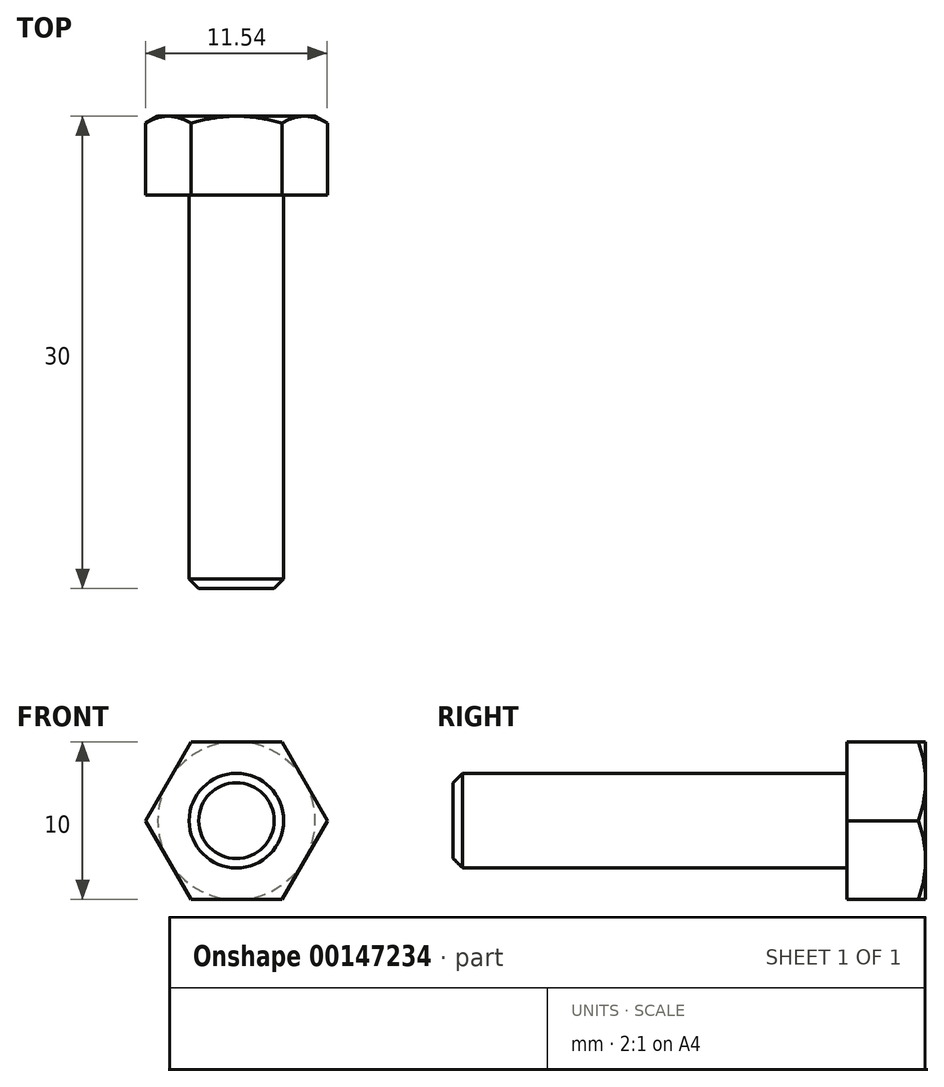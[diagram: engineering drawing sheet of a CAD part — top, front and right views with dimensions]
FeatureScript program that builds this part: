
annotation { "Feature Type Name" : "Feature", "Feature Type Description" : "" }
export const myFeature = defineFeature(function(context is Context, id is Id, definition is map)
    precondition{}
    {
        {
            var Q0;
            Q0=qCreatedBy(makeId("Front.planeOp"),FACE);
            var sketch = newSketch(context, id + "F0", { "sketchPlane" : qUnion([Q0])});
            skCircle(sketch, "E0.cCircle", {"center": v(0, 0) * mm, "radius": 5 * mm, "construction": true});
            skLineSegment(sketch, "E0.0", {"start": v(5.77, 0) * mm, "end": v(2.89, -5) * mm});
            skLineSegment(sketch, "E0.1", {"start": v(2.89, -5) * mm, "end": v(-2.89, -5) * mm});
            skLineSegment(sketch, "E0.2", {"start": v(-2.89, -5) * mm, "end": v(-5.77, 0) * mm});
            skLineSegment(sketch, "E0.3", {"start": v(-5.77, 0) * mm, "end": v(-2.89, 5) * mm});
            skLineSegment(sketch, "E0.4", {"start": v(-2.89, 5) * mm, "end": v(2.89, 5) * mm});
            skLineSegment(sketch, "E0.5", {"start": v(2.89, 5) * mm, "end": v(5.77, 0) * mm});
            skPoint(sketch, "E0.0.midPoint", {"position": v(4.33, -2.5) * mm});
            skSolve(sketch);
        }
        {
            var Q0;
            Q0 = qSketchRegion(id + "F0", true);
            extrude(context, id + "F1", {"entities" : qUnion([Q0]), "depth" : 5 * mm});
        }
        {
            var Q0;
            Q0=makeQuery(id+"F1.opExtrude","CAP_FACE",FACE,{"disambiguationData":[OSD([sQuery(id+"F0.wireOp",EDGE,"E0.0"),sQuery(id+"F0.wireOp",EDGE,"E0.1"),sQuery(id+"F0.wireOp",EDGE,"E0.2"),sQuery(id+"F0.wireOp",EDGE,"E0.3"),sQuery(id+"F0.wireOp",EDGE,"E0.4"),sQuery(id+"F0.wireOp",EDGE,"E0.5")])],"isStart":false});
            var sketch = newSketch(context, id + "F2", { "sketchPlane" : qUnion([Q0])});
            skCircle(sketch, "E1", {"center": v(0, 0) * mm, "radius": 3 * mm});
            skSolve(sketch);
        }
        {
            var Q0;
            Q0 = qSketchRegion(id + "F2", true);
            extrude(context, id + "F3", {"entities" : qUnion([Q0]), "operationType" : NewBodyOperationType.ADD, "depth" : 25 * mm});
        }
        {
            var Q0;
            Q0=makeQuery(id+"F3.opExtrude","CAP_EDGE",EDGE,{"disambiguationData":[OSD([sQuery(id+"F2.wireOp",EDGE,"E1")])],"isStart":false});
            chamfer(context, id + "F4", {"entities" : qUnion([Q0]), "width" : .6 * mm, "tangentPropagation" : true});
        }
        {
            var Q0;
            Q0=qCreatedBy(makeId("Right.planeOp"),FACE);
            var sketch = newSketch(context, id + "F5", { "sketchPlane" : qUnion([Q0])});
            skLineSegment(sketch, "E2", {"start": v(-2, -8.46) * mm, "end": v(2, -1.54) * mm});
            skLineSegment(sketch, "E3", {"start": v(2, -8.46) * mm, "end": v(2, -1.54) * mm});
            skLineSegment(sketch, "E4", {"start": v(2, -8.46) * mm, "end": v(-2, -8.46) * mm});
            skSolve(sketch);
        }
        {
            var Q0;
            Q0 = qSketchRegion(id + "F5", true);
            var Q1;
            Q1=makeQuery(id+"F3.opExtrude","SWEPT_FACE",FACE,{"disambiguationData":[OSD([sQuery(id+"F2.wireOp",EDGE,"E1")])]});
            revolve(context, id + "F6", {"operationType" : NewBodyOperationType.REMOVE, "entities" : qUnion([Q0]), "axis" : qUnion([Q1]), "revolveType" : RevolveType.FULL, "oppositeDirection" : true});
        }
    });
